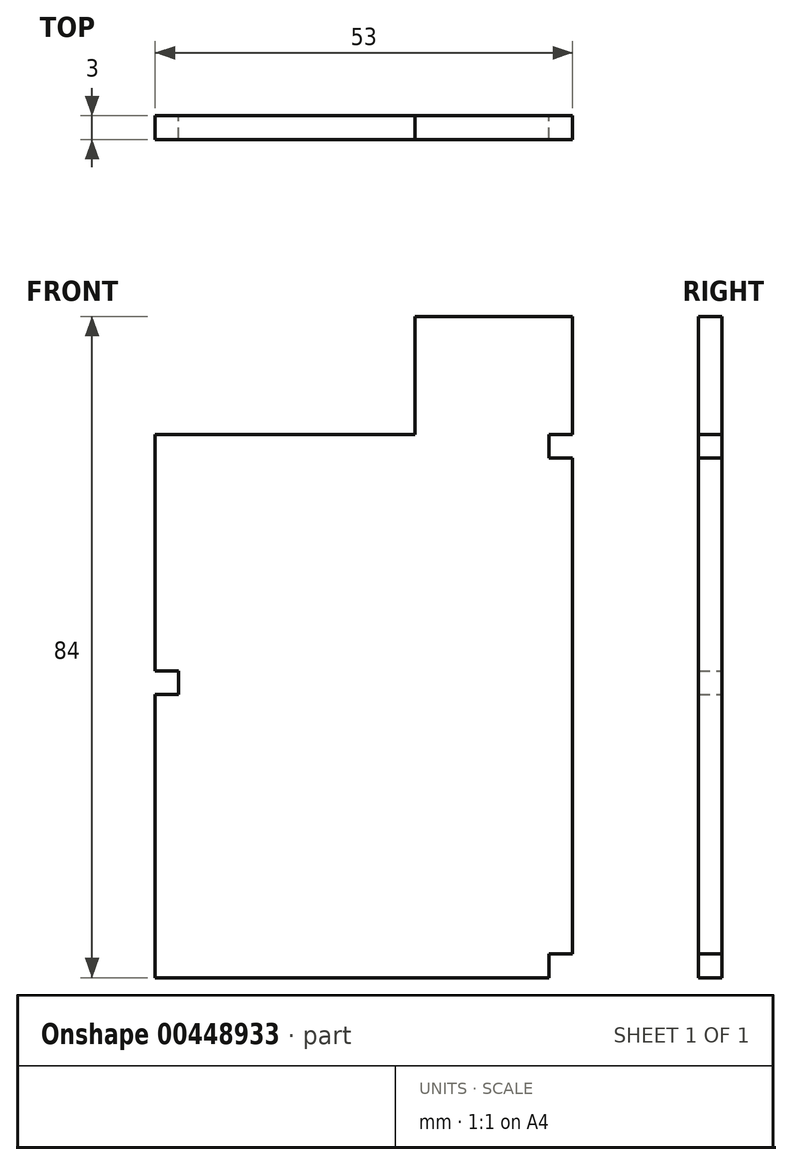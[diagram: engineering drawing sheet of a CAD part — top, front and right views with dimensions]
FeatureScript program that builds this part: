
annotation { "Feature Type Name" : "Feature", "Feature Type Description" : "" }
export const myFeature = defineFeature(function(context is Context, id is Id, definition is map)
    precondition{}
    {
        {
            var Q0;
            Q0=qCreatedBy(makeId("Front.planeOp"),FACE);
            var sketch = newSketch(context, id + "F0", { "sketchPlane" : qUnion([Q0])});
            skLineSegment(sketch, "E0", {"start": v(0, 0) * mm, "end": v(50, 0) * mm});
            skLineSegment(sketch, "E1", {"start": v(50, 0) * mm, "end": v(50, 3) * mm});
            skLineSegment(sketch, "E2", {"start": v(50, 3) * mm, "end": v(53, 3) * mm});
            skLineSegment(sketch, "E3", {"start": v(53, 3) * mm, "end": v(53, 66) * mm});
            skLineSegment(sketch, "E4", {"start": v(53, 66) * mm, "end": v(50, 66) * mm});
            skLineSegment(sketch, "E5", {"start": v(50, 66) * mm, "end": v(50, 69) * mm});
            skLineSegment(sketch, "E6", {"start": v(50, 69) * mm, "end": v(53, 69) * mm});
            skLineSegment(sketch, "E7", {"start": v(53, 69) * mm, "end": v(53, 84) * mm});
            skLineSegment(sketch, "E8", {"start": v(53, 84) * mm, "end": v(33, 84) * mm});
            skLineSegment(sketch, "E9", {"start": v(33, 84) * mm, "end": v(33, 69) * mm});
            skLineSegment(sketch, "E10", {"start": v(33, 69) * mm, "end": v(0, 69) * mm});
            skLineSegment(sketch, "E11", {"start": v(0, 69) * mm, "end": v(0, 39) * mm});
            skLineSegment(sketch, "E12", {"start": v(0, 39) * mm, "end": v(3, 39) * mm});
            skLineSegment(sketch, "E13", {"start": v(3, 39) * mm, "end": v(3, 36) * mm});
            skLineSegment(sketch, "E14", {"start": v(3, 36) * mm, "end": v(0, 36) * mm});
            skLineSegment(sketch, "E15", {"start": v(0, 36) * mm, "end": v(0, 0) * mm});
            skSolve(sketch);
        }
        {
            var Q0;
            Q0 = qSketchRegion(id + "F0", true);
            extrude(context, id + "F1", {"entities" : qUnion([Q0]), "depth" : 3 * mm});
        }
    });
